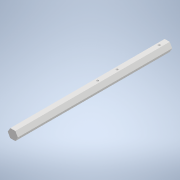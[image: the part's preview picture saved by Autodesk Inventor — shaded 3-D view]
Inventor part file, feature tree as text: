
AUTODESK INVENTOR PART (.ipt)
format: ipt  version: 2022 (Build 260153000, 153)  size: 122,368 bytes
history: native  units: mm
features: extrude x2, sketch x2
ambient origin geometry x8: Origin, YZ Plane, XZ Plane, XY Plane, X Axis, Y Axis, Z Axis, Center Point
bodies: Body1 (feature_tree)
feature tree (4):
  extrude  "Extrusion5"  Depth=3.1mm TaperAngle=360.0deg
  extrude  "Extrusion6"  Depth=95.0mm
  sketch  "Sketch7"  dims[d17=3.1mm d18=60.0mm d20=360.0deg]
  sketch  "Sketch8"  dims[d22=95.0mm d23=0.0mm d24=1.3mm d25=64.1mm d26=52.1mm d27=6.0mm d28=0.0mm d29=5.0mm d7=0.5mm d8=0.872665mm d9=0.5mm d10=0.872665mm]
